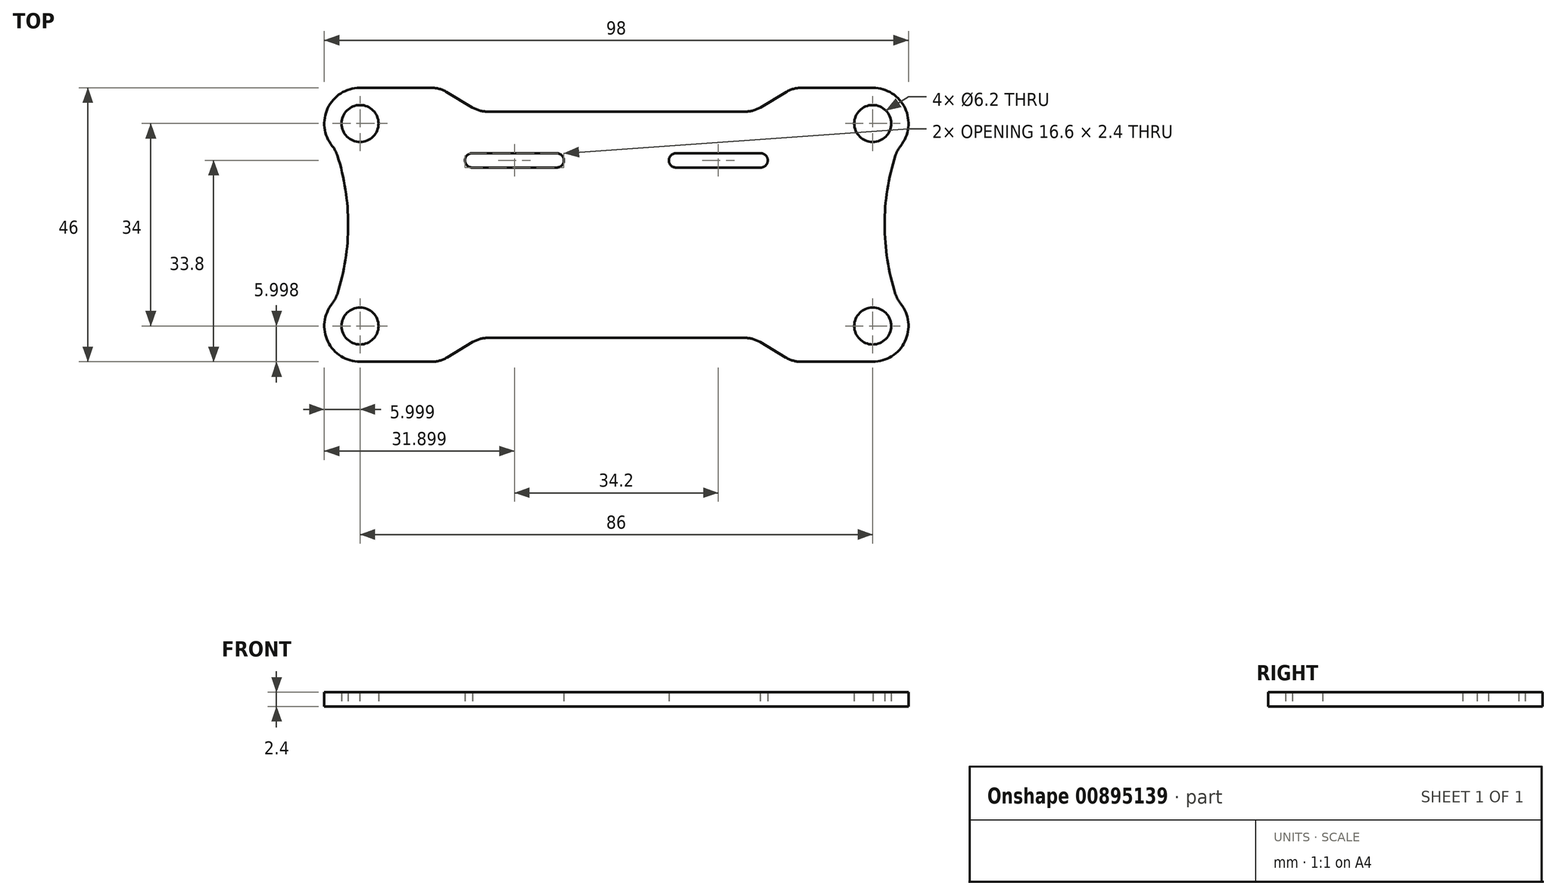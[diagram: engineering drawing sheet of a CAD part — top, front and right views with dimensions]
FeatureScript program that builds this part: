
annotation { "Feature Type Name" : "Feature", "Feature Type Description" : "" }
export const myFeature = defineFeature(function(context is Context, id is Id, definition is map)
    precondition{}
    {
        {
            var Q0;
            Q0=qCreatedBy(makeId("Top.planeOp"),FACE);
            var sketch = newSketch(context, id + "F0", { "sketchPlane" : qUnion([Q0])});
            skCircle(sketch, "E0", {"center": v(-47.28, 45.45) * mm, "radius": 3.1 * mm});
            skArc(sketch, "E1", {"start": v(-51.46, 15.76) * mm, "mid": v(-52.84, 9.2) * mm, "end": v(-47.28, 5.45) * mm});
            skArc(sketch, "E2", {"start": v(-47.21, 51.45) * mm, "mid": v(-52.83, 47.72) * mm, "end": v(-51.44, 41.12) * mm});
            skLineSegment(sketch, "E3", {"start": v(-49.28, 28.46) * mm, "end": v(-49.28, 28.47) * mm});
            skLineSegment(sketch, "E4", {"start": v(-47.35, 51.45) * mm, "end": v(-33.95, 51.45) * mm});
            skArc(sketch, "E5", {"start": v(-51.46, 15.76) * mm, "mid": v(-49.28, 28.44) * mm, "end": v(-51.44, 41.12) * mm});
            skPoint(sketch, "E6.orphan", {"position": v(-47.28, 14.36) * mm});
            skPoint(sketch, "E7.start.orphan", {"position": v(-47.28, 28.36) * mm});
            skPoint(sketch, "E8.orphan", {"position": v(-47.28, 42.35) * mm});
            skLineSegment(sketch, "E9", {"start": v(-47.28, 5.45) * mm, "end": v(-33.88, 5.45) * mm});
            skLineSegment(sketch, "E10", {"start": v(-4.28, 45.45) * mm, "end": v(-4.28, 11.45) * mm});
            skLineSegment(sketch, "E11", {"start": v(-27.28, 47.45) * mm, "end": v(-33.95, 51.45) * mm});
            skLineSegment(sketch, "E12", {"start": v(-27.21, 9.45) * mm, "end": v(-33.88, 5.45) * mm});
            skLineSegment(sketch, "E13", {"start": v(-26.08, 40.45) * mm, "end": v(-14.28, 40.45) * mm});
            skArc(sketch, "E14", {"start": v(-14.28, 38.05) * mm, "mid": v(-13.08, 39.25) * mm, "end": v(-14.28, 40.45) * mm});
            skLineSegment(sketch, "E15", {"start": v(-26.07, 38.05) * mm, "end": v(-14.28, 38.05) * mm});
            skPoint(sketch, "E16.end.orphan", {"position": v(-27.28, 11.45) * mm});
            skPoint(sketch, "E17.orphan", {"position": v(-44.18, 45.45) * mm});
            skPoint(sketch, "E18.orphan", {"position": v(35.62, 45.45) * mm});
            skLineSegment(sketch, "E19", {"start": v(-4.28, 45.45) * mm, "end": v(-4.28, 47.45) * mm});
            skLineSegment(sketch, "E20", {"start": v(-4.28, 47.45) * mm, "end": v(-27.28, 47.45) * mm});
            skLineSegment(sketch, "E21", {"start": v(-4.28, 11.45) * mm, "end": v(-4.28, 9.45) * mm});
            skLineSegment(sketch, "E22", {"start": v(-4.28, 9.45) * mm, "end": v(-27.21, 9.45) * mm});
            skPoint(sketch, "E23.orphan", {"position": v(-23.88, 11.45) * mm});
            skCircle(sketch, "E24", {"center": v(-47.28, 11.45) * mm, "radius": 3.1 * mm});
            skArc(sketch, "E25", {"start": v(-28.43, 40.45) * mm, "mid": v(-29.68, 39.27) * mm, "end": v(-28.47, 38.05) * mm});
            skLineSegment(sketch, "E26", {"start": v(-28.43, 40.45) * mm, "end": v(-26.08, 40.45) * mm});
            skLineSegment(sketch, "E27", {"start": v(-28.47, 38.05) * mm, "end": v(-26.07, 38.05) * mm});
            skArc(sketch, "E28.trimOffspring", {"start": v(-26.1, 38.05) * mm, "mid": v(-26.08, 38.05) * mm, "end": v(-26.07, 38.05) * mm});
            skLineSegment(sketch, "E29.trimOffspring", {"start": v(-27.28, 39.25) * mm, "end": v(-27.28, 39.25) * mm});
            skSolve(sketch);
        }
        {
            var Q0;
            Q0=makeQuery(id+"F0.imprint","IMPRINT",FACE,{"disambiguationData":[TD([[makeQuery(id+"F0.imprint","IMPRINT",EDGE,{"derivedFrom":sQuery(id+"F0.wireOp",EDGE,"E0")}),-1.0]])]});
            extrude(context, id + "F1", {"entities" : qUnion([Q0]), "depth" : 2.4 * mm});
        }
        {
            var Q0;
            Q0=makeQuery(id+"F1.opExtrude","SWEPT_BODY",BODY,{"disambiguationData":[OSD([sQuery(id+"F0.wireOp",EDGE,"E0"),sQuery(id+"F0.wireOp",EDGE,"PlCD5O4k-DVeD-ACMK-cPxN-HWvn4VUDhi4X"),sQuery(id+"F0.wireOp",EDGE,"E1"),sQuery(id+"F0.wireOp",EDGE,"E2"),sQuery(id+"F0.wireOp",EDGE,"E4"),sQuery(id+"F0.wireOp",EDGE,"E5"),sQuery(id+"F0.wireOp",EDGE,"E9"),sQuery(id+"F0.wireOp",EDGE,"E10"),sQuery(id+"F0.wireOp",EDGE,"E11"),sQuery(id+"F0.wireOp",EDGE,"E12"),sQuery(id+"F0.wireOp",EDGE,"E13"),sQuery(id+"F0.wireOp",EDGE,"wuIxOw39-Tq2w-nizm-UWeU-m0hKjEc662TV"),sQuery(id+"F0.wireOp",EDGE,"E14"),sQuery(id+"F0.wireOp",EDGE,"E15"),sQuery(id+"F0.wireOp",EDGE,"E19"),sQuery(id+"F0.wireOp",EDGE,"E20"),sQuery(id+"F0.wireOp",EDGE,"E21"),sQuery(id+"F0.wireOp",EDGE,"E22")])]});
            var Q1;
            Q1=makeQuery(id+"F1.opExtrude","SWEPT_FACE",FACE,{"disambiguationData":[OSD([sQuery(id+"F0.wireOp",EDGE,"E10"),sQuery(id+"F0.wireOp",EDGE,"E19"),sQuery(id+"F0.wireOp",EDGE,"E21")])]});
            mirror(context, id + "F2", {"operationType" : NewBodyOperationType.ADD, "entities" : qUnion([Q0]), "mirrorPlane" : qUnion([Q1])});
        }
        {
            var Q0;
            Q0=makeQuery(id+"F1.opExtrude","SWEPT_EDGE",EDGE,{"disambiguationData":[OSD([sQuery(id+"F0.wireOp",EDGE,"E4"),sQuery(id+"F0.wireOp",EDGE,"E11")])]});
            var Q1;
            Q1=makeQuery(id+"F1.opExtrude","SWEPT_EDGE",EDGE,{"disambiguationData":[OSD([sQuery(id+"F0.wireOp",EDGE,"E11"),sQuery(id+"F0.wireOp",EDGE,"E20")])]});
            var Q2;
            Q2=makeQuery(id+"F2.opPattern","COPY",EDGE,{"derivedFrom":makeQuery(id+"F1.opExtrude","SWEPT_EDGE",EDGE,{"disambiguationData":[OSD([sQuery(id+"F0.wireOp",EDGE,"E11"),sQuery(id+"F0.wireOp",EDGE,"E20")])]}),"instanceName":"1"});
            var Q3;
            Q3=makeQuery(id+"F2.opPattern","COPY",EDGE,{"derivedFrom":makeQuery(id+"F1.opExtrude","SWEPT_EDGE",EDGE,{"disambiguationData":[OSD([sQuery(id+"F0.wireOp",EDGE,"E4"),sQuery(id+"F0.wireOp",EDGE,"E11")])]}),"instanceName":"1"});
            var Q4;
            Q4=makeQuery(id+"F1.opExtrude","SWEPT_EDGE",EDGE,{"disambiguationData":[OSD([sQuery(id+"F0.wireOp",EDGE,"E9"),sQuery(id+"F0.wireOp",EDGE,"E12")])]});
            var Q5;
            Q5=makeQuery(id+"F1.opExtrude","SWEPT_EDGE",EDGE,{"disambiguationData":[OSD([sQuery(id+"F0.wireOp",EDGE,"E12"),sQuery(id+"F0.wireOp",EDGE,"E22")])]});
            var Q6;
            Q6=makeQuery(id+"F2.opPattern","COPY",EDGE,{"derivedFrom":makeQuery(id+"F1.opExtrude","SWEPT_EDGE",EDGE,{"disambiguationData":[OSD([sQuery(id+"F0.wireOp",EDGE,"E12"),sQuery(id+"F0.wireOp",EDGE,"E22")])]}),"instanceName":"1"});
            var Q7;
            Q7=makeQuery(id+"F2.opPattern","COPY",EDGE,{"derivedFrom":makeQuery(id+"F1.opExtrude","SWEPT_EDGE",EDGE,{"disambiguationData":[OSD([sQuery(id+"F0.wireOp",EDGE,"E9"),sQuery(id+"F0.wireOp",EDGE,"E12")])]}),"instanceName":"1"});
            var Q8;
            Q8=makeQuery(id+"F1.opExtrude","SWEPT_EDGE",EDGE,{"disambiguationData":[OSD([sQuery(id+"F0.wireOp",EDGE,"E1"),sQuery(id+"F0.wireOp",EDGE,"E5")])]});
            var Q9;
            Q9=makeQuery(id+"F1.opExtrude","SWEPT_EDGE",EDGE,{"disambiguationData":[OSD([sQuery(id+"F0.wireOp",EDGE,"E2"),sQuery(id+"F0.wireOp",EDGE,"E5")])]});
            var Q10;
            Q10=makeQuery(id+"F2.opPattern","COPY",EDGE,{"derivedFrom":makeQuery(id+"F1.opExtrude","SWEPT_EDGE",EDGE,{"disambiguationData":[OSD([sQuery(id+"F0.wireOp",EDGE,"E1"),sQuery(id+"F0.wireOp",EDGE,"E5")])]}),"instanceName":"1"});
            var Q11;
            Q11=makeQuery(id+"F2.opPattern","COPY",EDGE,{"derivedFrom":makeQuery(id+"F1.opExtrude","SWEPT_EDGE",EDGE,{"disambiguationData":[OSD([sQuery(id+"F0.wireOp",EDGE,"E2"),sQuery(id+"F0.wireOp",EDGE,"E5")])]}),"instanceName":"1"});
            fillet(context, id + "F3", {"entities" : qUnion([Q0, Q1, Q2, Q3, Q4, Q5, Q6, Q7, Q8, Q9, Q10, Q11]), "radius" : 5 * mm, "tangentPropagation" : true, "allowEdgeOverflow" : false});
        }
    });
